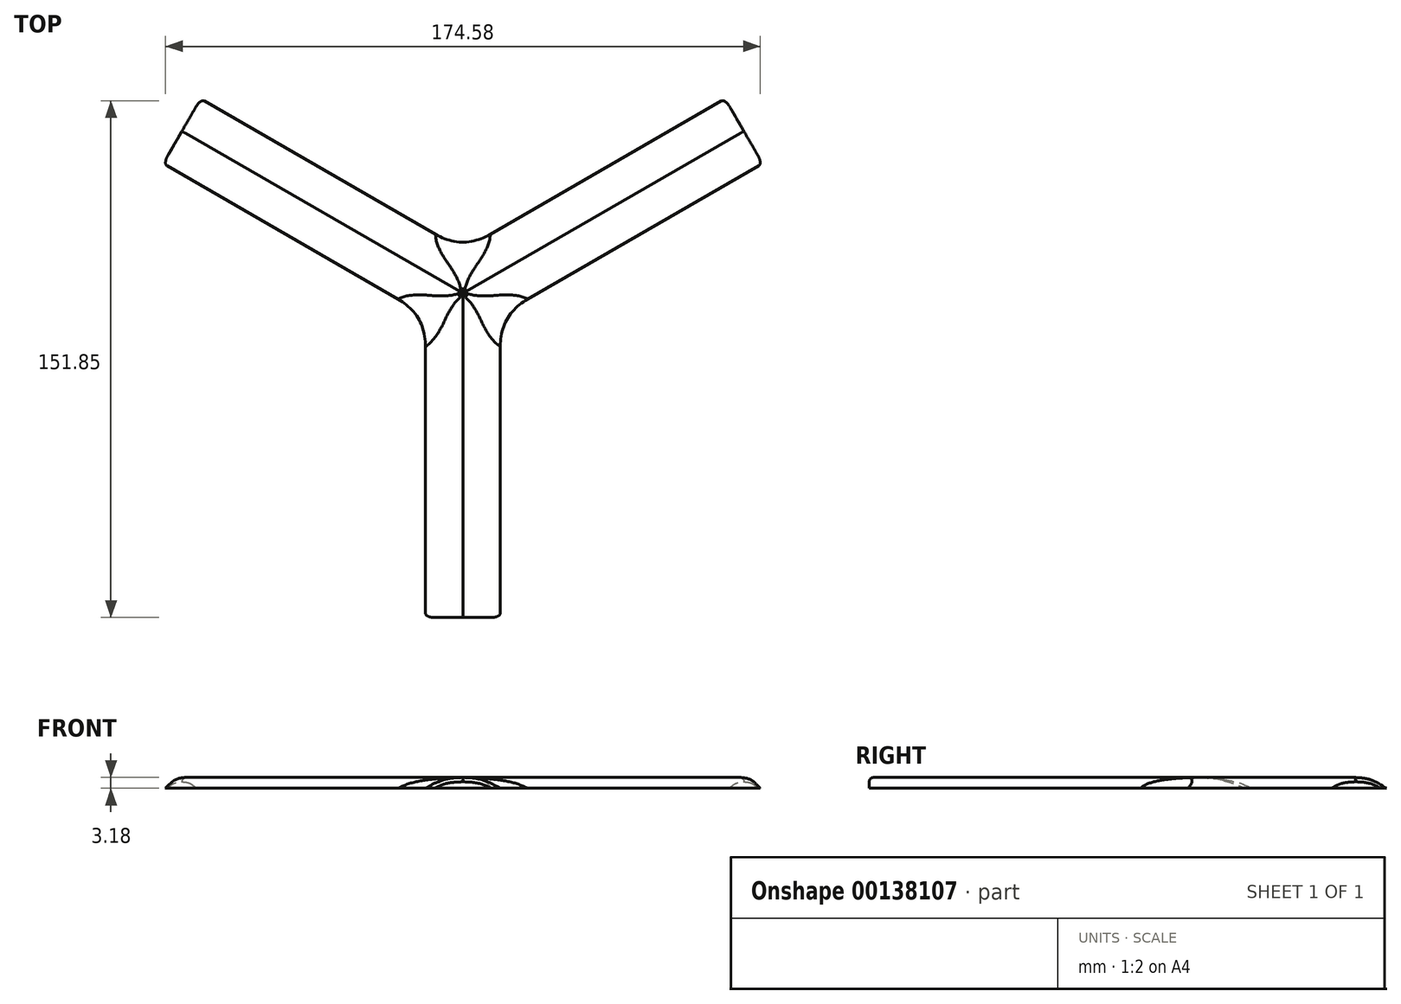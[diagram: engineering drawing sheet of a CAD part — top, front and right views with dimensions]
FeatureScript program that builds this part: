
annotation { "Feature Type Name" : "Feature", "Feature Type Description" : "" }
export const myFeature = defineFeature(function(context is Context, id is Id, definition is map)
    precondition{}
    {
        {
            var Q0;
            Q0=qCreatedBy(makeId("Top.planeOp"),FACE);
            var sketch = newSketch(context, id + "F0", { "sketchPlane" : qUnion([Q0])});
            skCircle(sketch, "E0.cCircle", {"center": v(0, 0) * mm, "radius": 6.35 * mm, "construction": true});
            skLineSegment(sketch, "E0.0", {"start": v(11, -6.35) * mm, "end": v(-11, -6.35) * mm});
            skLineSegment(sketch, "E0.1", {"start": v(-11, -6.35) * mm, "end": v(0, 12.7) * mm});
            skLineSegment(sketch, "E0.2", {"start": v(0, 12.7) * mm, "end": v(11, -6.35) * mm});
            skPoint(sketch, "E0.0.midPoint", {"position": v(0, -6.35) * mm});
            skSolve(sketch);
        }
        {
            var Q0;
            Q0=makeQuery(id+"F0.imprint","IMPRINT",FACE,{"disambiguationData":[TD([[makeQuery(id+"F0.imprint","IMPRINT",EDGE,{"derivedFrom":sQuery(id+"F0.wireOp",EDGE,"E0.0")}),-1.0]])]});
            extrude(context, id + "F1", {"entities" : qUnion([Q0]), "depth" : 3.17 * mm});
        }
        {
            var Q0;
            Q0=makeQuery(id+"F1.opExtrude","SWEPT_FACE",FACE,{"disambiguationData":[OSD([sQuery(id+"F0.wireOp",EDGE,"E0.0")])]});
            var sketch = newSketch(context, id + "F2", { "sketchPlane" : qUnion([Q0])});
            skLineSegment(sketch, "E1", {"start": v(0, 0) * mm, "end": v(0, 3.18) * mm, "construction": true});
            skLineSegment(sketch, "E2", {"start": v(0, 0) * mm, "end": v(-11, 0) * mm});
            skPoint(sketch, "E3.1.internal.snap0", {"position": v(-5.5, 0) * mm});
            skPoint(sketch, "E3.1.internal.snap1", {"position": v(0, 1.59) * mm});
            skLineSegment(sketch, "E4", {"start": v(-11, 0) * mm, "end": v(11, 0) * mm});
            skLineSegment(sketch, "E5", {"start": v(-5.5, 0) * mm, "end": v(-5.5, 2.54) * mm});
            skFitSpline(sketch, "E6", {"points": [v(-11, 0) * mm, v(-5.5, 2.54) * mm, v(0, 3.18) * mm], "startDerivative": vector(10.63, 5.9) * mm, "endDerivative": vector(11.37, 0.4) * mm});
            skFitSpline(sketch, "E7.MirrorCS", {"points": [v(11, 0) * mm, v(5.5, 2.54) * mm, v(0, 3.18) * mm], "startDerivative": vector(-10.63, 5.9) * mm, "endDerivative": vector(-11.37, 0.4) * mm});
            skSolve(sketch);
        }
        {
            var Q0;
            Q0=qSketchRegion(id+"F2",true);
            extrude(context, id + "F3", {"entities" : qUnion([Q0]), "operationType" : NewBodyOperationType.ADD, "depth" : 88.9 * mm});
        }
        {
            var Q0;
            Q0=makeQuery(id+"F1.opExtrude","SWEPT_FACE",FACE,{"disambiguationData":[OSD([sQuery(id+"F0.wireOp",EDGE,"E0.1")])]});
            var sketch = newSketch(context, id + "F4", { "sketchPlane" : qUnion([Q0])});
            skLineSegment(sketch, "E8", {"start": v(11, 0) * mm, "end": v(-11, 0) * mm});
            skLineSegment(sketch, "E9", {"start": v(-11, 0) * mm, "end": v(0, 0) * mm});
            skLineSegment(sketch, "E10", {"start": v(-5.5, 0) * mm, "end": v(-5.5, 2.54) * mm});
            skFitSpline(sketch, "E11", {"points": [v(-11, 0) * mm, v(-5.5, 2.54) * mm, v(0, 3.18) * mm], "startDerivative": vector(10.63, 5.9) * mm, "endDerivative": vector(11.37, 0.4) * mm});
            skLineSegment(sketch, "E12", {"start": v(0, 0) * mm, "end": v(0, 3.18) * mm});
            skFitSpline(sketch, "E13.MirrorCS", {"points": [v(11, 0) * mm, v(5.5, 2.54) * mm, v(0, 3.18) * mm], "startDerivative": vector(-10.63, 5.9) * mm, "endDerivative": vector(-11.37, 0.4) * mm});
            skSolve(sketch);
        }
        {
            var Q0;
            Q0=qSketchRegion(id+"F4",true);
            extrude(context, id + "F5", {"entities" : qUnion([Q0]), "operationType" : NewBodyOperationType.ADD, "depth" : 88.9 * mm});
        }
        {
            var Q0;
            Q0=makeQuery(id+"F1.opExtrude","SWEPT_FACE",FACE,{"disambiguationData":[OSD([sQuery(id+"F0.wireOp",EDGE,"E0.2")])]});
            var sketch = newSketch(context, id + "F6", { "sketchPlane" : qUnion([Q0])});
            skLineSegment(sketch, "E14", {"start": v(0, 0) * mm, "end": v(0, 3.18) * mm});
            skLineSegment(sketch, "E15", {"start": v(0, 0) * mm, "end": v(-11, 0) * mm});
            skLineSegment(sketch, "E16", {"start": v(-5.5, 0) * mm, "end": v(-5.5, 2.54) * mm});
            skFitSpline(sketch, "E17", {"points": [v(-11, 0) * mm, v(-5.5, 2.54) * mm, v(0, 3.18) * mm], "startDerivative": vector(10.63, 5.9) * mm, "endDerivative": vector(11.37, 0.4) * mm});
            skFitSpline(sketch, "E18.MirrorCS", {"points": [v(11, 0) * mm, v(5.5, 2.54) * mm, v(0, 3.18) * mm], "startDerivative": vector(-10.63, 5.9) * mm, "endDerivative": vector(-11.37, 0.4) * mm});
            skLineSegment(sketch, "E19", {"start": v(0, 0) * mm, "end": v(11, 0) * mm});
            skSolve(sketch);
        }
        {
            var Q0;
            Q0=qSketchRegion(id+"F6",true);
            extrude(context, id + "F7", {"entities" : qUnion([Q0]), "operationType" : NewBodyOperationType.ADD, "depth" : 88.9 * mm});
        }
        {
            var Q0;
            Q0=makeQuery(id+"F1.opExtrude","CAP_FACE",FACE,{"disambiguationData":[OSD([sQuery(id+"F0.wireOp",EDGE,"E0.0"),sQuery(id+"F0.wireOp",EDGE,"E0.1"),sQuery(id+"F0.wireOp",EDGE,"E0.2")])],"isStart":false});
            var sketch = newSketch(context, id + "F8", { "sketchPlane" : qUnion([Q0])});
            skLineSegment(sketch, "E20", {"start": v(11, -6.35) * mm, "end": v(-11, -6.35) * mm});
            skLineSegment(sketch, "E21", {"start": v(-11, -6.35) * mm, "end": v(0, 12.7) * mm});
            skLineSegment(sketch, "E22", {"start": v(0, 12.7) * mm, "end": v(11, -6.35) * mm});
            skSolve(sketch);
        }
        {
            var Q0;
            Q0=qSketchRegion(id+"F8",true);
            extrude(context, id + "F9", {"entities" : qUnion([Q0]), "operationType" : NewBodyOperationType.REMOVE, "endBound" : BoundingType.UP_TO_NEXT, "oppositeDirection" : true, "depth" : 25.4 * mm});
        }
        {
            var Q0;
            Q0=makeQuery(id+"F9.boolean.opBoolean","COPY",FACE,{"derivedFrom":makeQuery(id+"F9.opExtrude","SWEPT_FACE",FACE,{"disambiguationData":[OSD([sQuery(id+"F8.wireOp",EDGE,"E22")])]})});
            extrude(context, id + "F10", {"entities" : qUnion([Q0]), "depth" : 7.62 * mm});
        }
        {
            var Q0;
            Q0=makeQuery(id+"F9.boolean.opBoolean","COPY",FACE,{"derivedFrom":makeQuery(id+"F9.opExtrude","SWEPT_FACE",FACE,{"disambiguationData":[OSD([sQuery(id+"F8.wireOp",EDGE,"E20")])]})});
            extrude(context, id + "F11", {"entities" : qUnion([Q0]), "depth" : 7.62 * mm});
        }
        {
            var Q0;
            Q0=makeQuery(id+"F9.boolean.opBoolean","COPY",FACE,{"derivedFrom":makeQuery(id+"F9.opExtrude","SWEPT_FACE",FACE,{"disambiguationData":[OSD([sQuery(id+"F8.wireOp",EDGE,"E21")])]})});
            extrude(context, id + "F12", {"entities" : qUnion([Q0]), "depth" : 7.62 * mm});
        }
        {
            var Q0;
            Q0=makeQuery(id+"F11.opExtrude","SWEPT_BODY",BODY,{"disambiguationData":[OSD([sQuery(id+"F8.wireOp",EDGE,"E20")])]});
            var Q1;
            Q1=makeQuery(id+"F9.boolean.opBoolean","SPLIT",BODY,{"disambiguationData":[OD(0.0)],"derivedFrom":makeQuery(id+"F1.opExtrude","SWEPT_BODY",BODY,{"disambiguationData":[OSD([sQuery(id+"F0.wireOp",EDGE,"E0.0"),sQuery(id+"F0.wireOp",EDGE,"E0.1"),sQuery(id+"F0.wireOp",EDGE,"E0.2")])]})});
            var Q2;
            Q2=makeQuery(id+"F9.boolean.opBoolean","SPLIT",BODY,{"disambiguationData":[OD(2.0)],"derivedFrom":makeQuery(id+"F1.opExtrude","SWEPT_BODY",BODY,{"disambiguationData":[OSD([sQuery(id+"F0.wireOp",EDGE,"E0.0"),sQuery(id+"F0.wireOp",EDGE,"E0.1"),sQuery(id+"F0.wireOp",EDGE,"E0.2")])]})});
            var Q3;
            Q3=makeQuery(id+"F9.boolean.opBoolean","SPLIT",BODY,{"disambiguationData":[OD(1.0)],"derivedFrom":makeQuery(id+"F1.opExtrude","SWEPT_BODY",BODY,{"disambiguationData":[OSD([sQuery(id+"F0.wireOp",EDGE,"E0.0"),sQuery(id+"F0.wireOp",EDGE,"E0.1"),sQuery(id+"F0.wireOp",EDGE,"E0.2")])]})});
            var Q4;
            Q4=makeQuery(id+"F12.opExtrude","SWEPT_BODY",BODY,{"disambiguationData":[OSD([sQuery(id+"F8.wireOp",EDGE,"E21")])]});
            var Q5;
            Q5=makeQuery(id+"F10.opExtrude","SWEPT_BODY",BODY,{"disambiguationData":[OSD([sQuery(id+"F8.wireOp",EDGE,"E22")])]});
            booleanBodies(context, id + "F13", {"operationType" : BooleanOperationType.UNION, "tools" : qUnion([Q0, Q1, Q2, Q3, Q4, Q5])});
        }
        {
            var Q0;
            Q0=makeQuery(id+"F13.opBoolean","INTERSECT",EDGE,{"derivedFrom":[makeQuery(id+"F11.opExtrude","SWEPT_FACE",FACE,{"disambiguationData":[OSD([sQuery(id+"F2.wireOp",EDGE,"E6")])]}),makeQuery(id+"F12.opExtrude","SWEPT_FACE",FACE,{"disambiguationData":[OSD([sQuery(id+"F4.wireOp",EDGE,"E13.MirrorCS")])]})]});
            var Q1;
            Q1=makeQuery(id+"F13.opBoolean","INTERSECT",EDGE,{"derivedFrom":[makeQuery(id+"F10.opExtrude","SWEPT_FACE",FACE,{"disambiguationData":[OSD([sQuery(id+"F6.wireOp",EDGE,"E18.MirrorCS")])]}),makeQuery(id+"F12.opExtrude","SWEPT_FACE",FACE,{"disambiguationData":[OSD([sQuery(id+"F4.wireOp",EDGE,"E11")])]})]});
            var Q2;
            {var subQ0=sQuery(id+"F2.wireOp",EDGE,"E7.MirrorCS");Q2=makeQuery(id+"F13.opBoolean","INTERSECT",EDGE,{"derivedFrom":[makeQuery(id+"F3.opExtrude","SWEPT_FACE",FACE,{"disambiguationData":[OSD([subQ0])]}),makeQuery(id+"F10.opExtrude","SWEPT_FACE",FACE,{"disambiguationData":[OSD([sQuery(id+"F6.wireOp",EDGE,"E17")])]}),makeQuery(id+"F11.opExtrude","SWEPT_FACE",FACE,{"disambiguationData":[OSD([subQ0])]})]});}
            fillet(context, id + "F14", {"entities" : qUnion([Q0, Q1, Q2]), "radius" : 33.02 * mm, "tangentPropagation" : true, "allowEdgeOverflow" : false});
        }
        {
            var Q0;
            Q0=makeQuery(id+"F7.opExtrude","CAP_EDGE",EDGE,{"disambiguationData":[OSD([sQuery(id+"F6.wireOp",EDGE,"E18.MirrorCS")])],"isStart":false});
            var Q1;
            Q1=makeQuery(id+"F7.opExtrude","CAP_EDGE",EDGE,{"disambiguationData":[OSD([sQuery(id+"F6.wireOp",EDGE,"E17")])],"isStart":false});
            var Q2;
            Q2=makeQuery(id+"F5.opExtrude","CAP_EDGE",EDGE,{"disambiguationData":[OSD([sQuery(id+"F4.wireOp",EDGE,"E13.MirrorCS")])],"isStart":false});
            var Q3;
            Q3=makeQuery(id+"F5.opExtrude","CAP_EDGE",EDGE,{"disambiguationData":[OSD([sQuery(id+"F4.wireOp",EDGE,"E11")])],"isStart":false});
            var Q4;
            Q4=makeQuery(id+"F3.opExtrude","CAP_EDGE",EDGE,{"disambiguationData":[OSD([sQuery(id+"F2.wireOp",EDGE,"E7.MirrorCS")])],"isStart":false});
            var Q5;
            Q5=makeQuery(id+"F3.opExtrude","CAP_EDGE",EDGE,{"disambiguationData":[OSD([sQuery(id+"F2.wireOp",EDGE,"E6")])],"isStart":false});
            fillet(context, id + "F15", {"entities" : qUnion([Q0, Q1, Q2, Q3, Q4, Q5]), "radius" : 1.27 * mm, "tangentPropagation" : true, "allowEdgeOverflow" : false});
        }
    });
